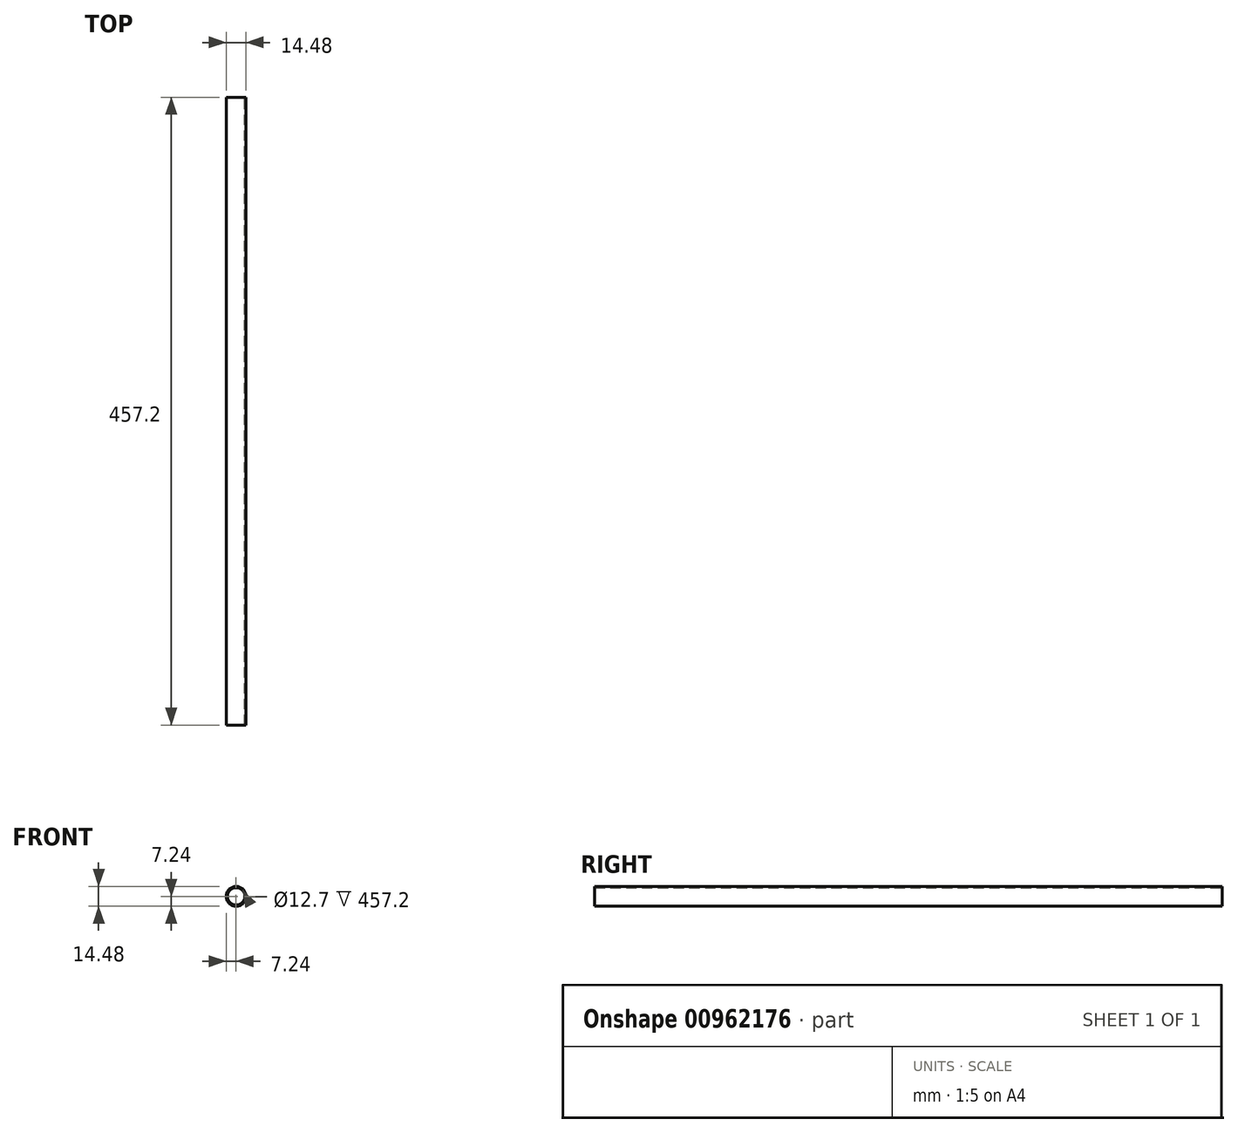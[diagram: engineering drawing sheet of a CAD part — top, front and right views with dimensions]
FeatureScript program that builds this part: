
annotation { "Feature Type Name" : "Feature", "Feature Type Description" : "" }
export const myFeature = defineFeature(function(context is Context, id is Id, definition is map)
    precondition{}
    {
        {
            var Q0;
            Q0=qCreatedBy(makeId("Front.planeOp"),FACE);
            var sketch = newSketch(context, id + "F0", { "sketchPlane" : qUnion([Q0])});
            skCircle(sketch, "E0", {"center": v(0, 0) * mm, "radius": 6.35 * mm});
            skCircle(sketch, "E1", {"center": v(0, 0) * mm, "radius": 7.24 * mm});
            skSolve(sketch);
        }
        {
            var Q0;
            Q0=makeQuery(id+"F0.imprint","IMPRINT",FACE,{"disambiguationData":[TD([[makeQuery(id+"F0.imprint","IMPRINT",EDGE,{"derivedFrom":sQuery(id+"F0.wireOp",EDGE,"E0")}),-1.0]])]});
            extrude(context, id + "F1", {"entities" : qUnion([Q0]), "depth" : 457.2 * mm, "offsetDistance" : 25.4 * mm});
        }
    });
